# Revit family: Edesso
name_source: partatom
category: Mechanical Equipment
units: mm (PartAtom-declared; Revit-internal decimal feet)

## family parameters
Always vertical = Yes
Cut with Voids When Loaded = No
OmniClass Number = 23.75.00.00
OmniClass Title = Climate Control (HVAC)
Part Type = Normal
Room Calculation Point = No
Round Connector Dimension = Use Diameter
Shared = No
Work Plane-Based = No

## types (6) — shared parameters
Aan/afvoer = Heating element connection 2 : 1"
Diameter aan/afvoer = 25 mm  [stored 0.082021 ft]
Manufacturer = Masterwatt B.V.
Materiaal 1 = Default New Material
Materiaal 2 = Kunststof zwart glimmend
URL = https://masterwatt.nl
zero-valued in all types: Default Elevation

## per-type parameters (varying)
| type | Art. No. | B | C | D | D Opening voor | Diameter (A) | Diameter uitlopen & circulatie | E | E Aansluiting voor | F | M | Model | N | Radius | Radius vat | Uitlopen & circulatie |
| 120 liter | 200 860 120 | 571 mm | 924 mm  [stored 3.0315 ft] | 203 mm | 338 mm  [stored 1.10892 ft] | 550 mm | 19 mm | 462 mm | 624 mm | 728 mm | 261 mm | Edesso 120 | 511 mm | 275 mm | 267 mm  [stored 0.875984 ft] | Heating element connection 2 : 3/4" |
| 160 liter | 200 860 160 | 571 mm | 1174 mm | 203 mm | 338 mm  [stored 1.10892 ft] | 550 mm | 19 mm | 591 mm | 874 mm | 978 mm | 261 mm | Edesso 160 | 721 mm | 275 mm | 267 mm  [stored 0.875984 ft] | Heating element connection 2 : 3/4" |
| 200 liter | 200 860 200 | 571 mm | 1524 mm | 203 mm | 338 mm  [stored 1.10892 ft] | 550 mm | 19 mm | 729 mm | 1224 mm | 1328 mm | 261 mm | Edesso 200 | 821 mm | 275 mm | 267 mm  [stored 0.875984 ft] | Heating element connection 2 : 3/4" |
| 300 liter | 200 860 300 | 698 mm | 1526 mm | 228 mm | 377 mm | 650 mm | 25 mm  [stored 0.082021 ft] | 803 mm | 1226 mm | 1283 mm | 279 mm | Edesso 300 | 859 mm | 325 mm  [stored 1.06627 ft] | 317 mm  [stored 1.04003 ft] | Heating element connection 2 : 1" |
| 400 liter | 200 860 400 | 798 mm  [stored 2.61811 ft] | 1530 mm | 263 mm  [stored 0.862861 ft] | 402 mm  [stored 1.3189 ft] | 750 mm  [stored 2.46063 ft] | 25 mm  [stored 0.082021 ft] | 763 mm | 1230 mm | 1248 mm | 361 mm | Edesso 400 | 811 mm | 375 mm  [stored 1.23031 ft] | 367 mm  [stored 1.20407 ft] | Heating element connection 2 : 1" |
| 500 liter | 200 860 500 | 798 mm  [stored 2.61811 ft] | 1796 mm | 263 mm  [stored 0.862861 ft] | 402 mm  [stored 1.3189 ft] | 750 mm  [stored 2.46063 ft] | 25 mm  [stored 0.082021 ft] | 913 mm | 1496 mm | 1513 mm | 361 mm | Edesso 500 | 946 mm | 375 mm  [stored 1.23031 ft] | 367 mm  [stored 1.20407 ft] | Heating element connection 2 : 1" |

note: [stored X ft] marks values corroborated as IEEE doubles in the binary element streams (Revit-internal decimal feet)

## geometry (parser evidence)
native form markers: Sweep x9
no freeform markers — native parametric forms only
